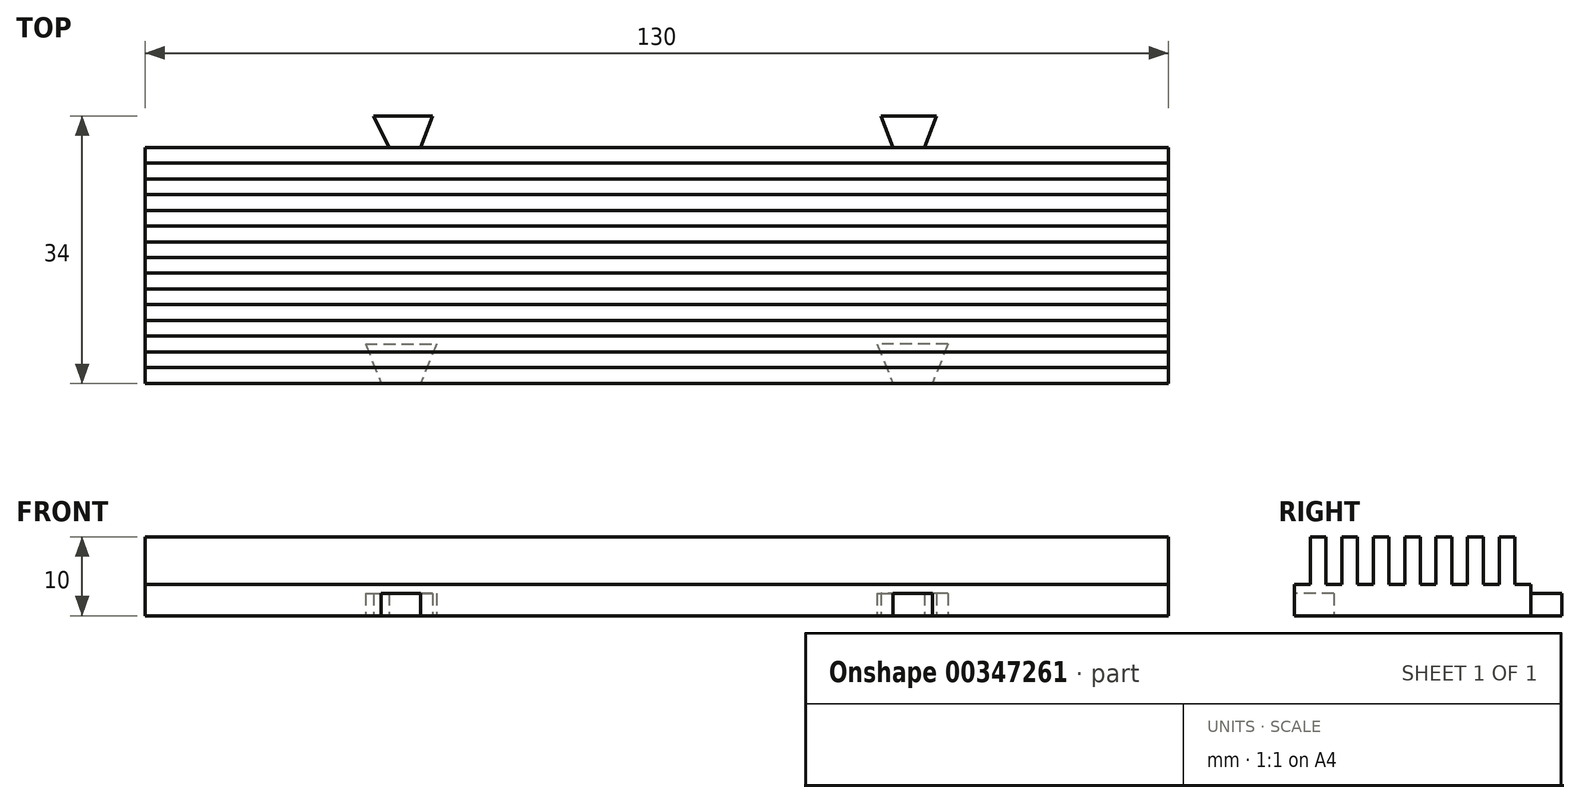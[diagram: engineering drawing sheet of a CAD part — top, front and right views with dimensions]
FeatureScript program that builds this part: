
annotation { "Feature Type Name" : "Feature", "Feature Type Description" : "" }
export const myFeature = defineFeature(function(context is Context, id is Id, definition is map)
    precondition{}
    {
        {
            var Q0;
            Q0=qCreatedBy(makeId("Top.planeOp"),FACE);
            var sketch = newSketch(context, id + "F0", { "sketchPlane" : qUnion([Q0])});
            skLineSegment(sketch, "E0.bottom", {"start": v(65, 15) * mm, "end": v(-65, 15) * mm});
            skLineSegment(sketch, "E0.top", {"start": v(65, -15) * mm, "end": v(-65, -15) * mm});
            skLineSegment(sketch, "E0.left", {"start": v(65, 15) * mm, "end": v(65, -15) * mm});
            skLineSegment(sketch, "E0.right", {"start": v(-65, 15) * mm, "end": v(-65, -15) * mm});
            skPoint(sketch, "E0.middle", {"position": v(0, 0) * mm});
            skSolve(sketch);
        }
        {
            var Q0;
            Q0=makeQuery(id+"F0.imprint","IMPRINT",FACE,{"disambiguationData":[TD([[makeQuery(id+"F0.imprint","IMPRINT",EDGE,{"derivedFrom":sQuery(id+"F0.wireOp",EDGE,"E0.bottom")}),1.0]])]});
            extrude(context, id + "F1", {"entities" : qUnion([Q0]), "depth" : 10 * mm});
        }
        {
            var Q0;
            Q0=makeQuery(id+"F1.opExtrude","CAP_FACE",FACE,{"disambiguationData":[OSD([sQuery(id+"F0.wireOp",EDGE,"E0.bottom"),sQuery(id+"F0.wireOp",EDGE,"E0.top"),sQuery(id+"F0.wireOp",EDGE,"E0.left"),sQuery(id+"F0.wireOp",EDGE,"E0.right")])],"isStart":false});
            var sketch = newSketch(context, id + "F2", { "sketchPlane" : qUnion([Q0])});
            skLineSegment(sketch, "E1", {"start": v(-65, -15) * mm, "end": v(-65, -13) * mm});
            skLineSegment(sketch, "E2", {"start": v(-65, -13) * mm, "end": v(65, -13) * mm});
            skLineSegment(sketch, "E3", {"start": v(65, -13) * mm, "end": v(65, -11) * mm});
            skLineSegment(sketch, "E4", {"start": v(65, -11) * mm, "end": v(-65, -11) * mm});
            skLineSegment(sketch, "E5", {"start": v(-65, -11) * mm, "end": v(-65, -9) * mm});
            skLineSegment(sketch, "E6", {"start": v(-65, -9) * mm, "end": v(65, -9) * mm});
            skLineSegment(sketch, "E7", {"start": v(65, -9) * mm, "end": v(65, -7) * mm});
            skLineSegment(sketch, "E8", {"start": v(65, -7) * mm, "end": v(-65, -7) * mm});
            skLineSegment(sketch, "E9", {"start": v(-65, -7) * mm, "end": v(-65, -5) * mm});
            skLineSegment(sketch, "E10", {"start": v(-65, -5) * mm, "end": v(65, -5) * mm});
            skLineSegment(sketch, "E11", {"start": v(65, -5) * mm, "end": v(65, -3) * mm});
            skLineSegment(sketch, "E12", {"start": v(65, -3) * mm, "end": v(-65, -3) * mm});
            skLineSegment(sketch, "E13", {"start": v(-65, -3) * mm, "end": v(-65, -1) * mm});
            skLineSegment(sketch, "E14", {"start": v(-65, -1) * mm, "end": v(65, -1) * mm});
            skLineSegment(sketch, "E15", {"start": v(65, -1) * mm, "end": v(65, 1) * mm});
            skLineSegment(sketch, "E16", {"start": v(65, 1) * mm, "end": v(-65, 1) * mm});
            skLineSegment(sketch, "E17", {"start": v(-65, 1) * mm, "end": v(-65, 3) * mm});
            skLineSegment(sketch, "E18", {"start": v(-65, 3) * mm, "end": v(65, 3) * mm});
            skLineSegment(sketch, "E19", {"start": v(65, 3) * mm, "end": v(65, 5) * mm});
            skLineSegment(sketch, "E20", {"start": v(65, 5) * mm, "end": v(-65, 5) * mm});
            skLineSegment(sketch, "E21", {"start": v(-65, 5) * mm, "end": v(-65, 7) * mm});
            skLineSegment(sketch, "E22", {"start": v(-65, 7) * mm, "end": v(65, 7) * mm});
            skLineSegment(sketch, "E23", {"start": v(65, 7) * mm, "end": v(65, 9) * mm});
            skLineSegment(sketch, "E24", {"start": v(65, 9) * mm, "end": v(-65, 9) * mm});
            skLineSegment(sketch, "E25", {"start": v(-65, 9) * mm, "end": v(-65, 11) * mm});
            skLineSegment(sketch, "E26", {"start": v(-65, 11) * mm, "end": v(65, 11) * mm});
            skLineSegment(sketch, "E27", {"start": v(65, 11) * mm, "end": v(65, 13) * mm});
            skLineSegment(sketch, "E28", {"start": v(65, 13) * mm, "end": v(-65, 13) * mm});
            skSolve(sketch);
        }
        {
            var Q0;
            Q0=makeQuery(id+"F2.imprint","IMPRINT",FACE,{"disambiguationData":[TD([[makeQuery(id+"F2.imprint","IMPRINT",EDGE,{"derivedFrom":sQuery(id+"F2.wireOp",EDGE,"E1")}),1.0]])]});
            var Q1;
            {var subQ0=sQuery(id+"F2.wireOp",EDGE,"E4");Q1=makeQuery(id+"F2.imprint","IMPRINT",FACE,{"disambiguationData":[TD([[makeQuery(id+"F2.imprint","IMPRINT",EDGE,{"derivedFrom":subQ0}),-1.0]])]});}
            var Q2;
            {var subQ0=sQuery(id+"F2.wireOp",EDGE,"E8");Q2=makeQuery(id+"F2.imprint","IMPRINT",FACE,{"disambiguationData":[TD([[makeQuery(id+"F2.imprint","IMPRINT",EDGE,{"derivedFrom":subQ0}),-1.0]])]});}
            var Q3;
            {var subQ0=sQuery(id+"F2.wireOp",EDGE,"E12");Q3=makeQuery(id+"F2.imprint","IMPRINT",FACE,{"disambiguationData":[TD([[makeQuery(id+"F2.imprint","IMPRINT",EDGE,{"derivedFrom":subQ0}),-1.0]])]});}
            var Q4;
            {var subQ0=sQuery(id+"F2.wireOp",EDGE,"E16");Q4=makeQuery(id+"F2.imprint","IMPRINT",FACE,{"disambiguationData":[TD([[makeQuery(id+"F2.imprint","IMPRINT",EDGE,{"derivedFrom":subQ0}),-1.0]])]});}
            var Q5;
            {var subQ0=sQuery(id+"F2.wireOp",EDGE,"E20");Q5=makeQuery(id+"F2.imprint","IMPRINT",FACE,{"disambiguationData":[TD([[makeQuery(id+"F2.imprint","IMPRINT",EDGE,{"derivedFrom":subQ0}),-1.0]])]});}
            var Q6;
            {var subQ0=sQuery(id+"F2.wireOp",EDGE,"E24");Q6=makeQuery(id+"F2.imprint","IMPRINT",FACE,{"disambiguationData":[TD([[makeQuery(id+"F2.imprint","IMPRINT",EDGE,{"derivedFrom":subQ0}),-1.0]])]});}
            var Q7;
            {var subQ0=sQuery(id+"F2.wireOp",EDGE,"E28");Q7=makeQuery(id+"F2.imprint","IMPRINT",FACE,{"disambiguationData":[TD([[makeQuery(id+"F2.imprint","IMPRINT",EDGE,{"derivedFrom":subQ0}),-1.0]])]});}
            extrude(context, id + "F3", {"entities" : qUnion([Q0, Q1, Q2, Q3, Q4, Q5, Q6, Q7]), "operationType" : NewBodyOperationType.REMOVE, "oppositeDirection" : true, "depth" : 6 * mm});
        }
        {
            var Q0;
            Q0=makeQuery(id+"F1.opExtrude","CAP_FACE",FACE,{"disambiguationData":[OSD([sQuery(id+"F0.wireOp",EDGE,"E0.bottom"),sQuery(id+"F0.wireOp",EDGE,"E0.top"),sQuery(id+"F0.wireOp",EDGE,"E0.left"),sQuery(id+"F0.wireOp",EDGE,"E0.right")])],"isStart":true});
            var sketch = newSketch(context, id + "F4", { "sketchPlane" : qUnion([Q0])});
            skLineSegment(sketch, "E29", {"start": v(-65, 15) * mm, "end": v(-35, 15) * mm});
            skLineSegment(sketch, "E30", {"start": v(-35, 15) * mm, "end": v(-30, 15) * mm});
            skLineSegment(sketch, "E31", {"start": v(-30, 15) * mm, "end": v(-30, 10) * mm});
            skLineSegment(sketch, "E32", {"start": v(-30, 10) * mm, "end": v(-28, 10) * mm});
            skLineSegment(sketch, "E33", {"start": v(-28, 10) * mm, "end": v(-30, 15) * mm});
            skLineSegment(sketch, "E34", {"start": v(-35, 15) * mm, "end": v(-35, 10) * mm});
            skLineSegment(sketch, "E35", {"start": v(-35, 10) * mm, "end": v(-37, 10) * mm});
            skLineSegment(sketch, "E36", {"start": v(-37, 10) * mm, "end": v(-35, 15) * mm});
            skLineSegment(sketch, "E37", {"start": v(-35, 10) * mm, "end": v(-30, 10) * mm});
            skLineSegment(sketch, "E38", {"start": v(65, 15) * mm, "end": v(35, 15) * mm});
            skLineSegment(sketch, "E39", {"start": v(35, 15) * mm, "end": v(30, 15) * mm});
            skLineSegment(sketch, "E40", {"start": v(30, 15) * mm, "end": v(30, 10) * mm});
            skLineSegment(sketch, "E41", {"start": v(30, 10) * mm, "end": v(28, 10) * mm});
            skLineSegment(sketch, "E42", {"start": v(28, 10) * mm, "end": v(30, 15) * mm});
            skLineSegment(sketch, "E43", {"start": v(35, 15) * mm, "end": v(35, 10) * mm});
            skLineSegment(sketch, "E44", {"start": v(35, 10) * mm, "end": v(37, 10) * mm});
            skLineSegment(sketch, "E45", {"start": v(37, 10) * mm, "end": v(35, 15) * mm});
            skLineSegment(sketch, "E46", {"start": v(35, 10) * mm, "end": v(30, 10) * mm});
            skLineSegment(sketch, "E47", {"start": v(-65, -15) * mm, "end": v(-34, -15) * mm});
            skLineSegment(sketch, "E48", {"start": v(-34, -15) * mm, "end": v(-30, -15) * mm});
            skLineSegment(sketch, "E49", {"start": v(-30, -15) * mm, "end": v(-30, -19) * mm});
            skLineSegment(sketch, "E50", {"start": v(-30, -19) * mm, "end": v(-28.5, -19) * mm});
            skLineSegment(sketch, "E51", {"start": v(-28.5, -19) * mm, "end": v(-30, -15) * mm});
            skLineSegment(sketch, "E52", {"start": v(-34, -15) * mm, "end": v(-34, -19) * mm});
            skLineSegment(sketch, "E53", {"start": v(-34, -19) * mm, "end": v(-36, -19) * mm});
            skLineSegment(sketch, "E54", {"start": v(-36, -19) * mm, "end": v(-34, -15) * mm});
            skLineSegment(sketch, "E55", {"start": v(-34, -19) * mm, "end": v(-30, -19) * mm});
            skLineSegment(sketch, "E56", {"start": v(65, -15) * mm, "end": v(34, -15) * mm});
            skLineSegment(sketch, "E57", {"start": v(34, -15) * mm, "end": v(30, -15) * mm});
            skLineSegment(sketch, "E58", {"start": v(30, -15) * mm, "end": v(30, -19) * mm});
            skLineSegment(sketch, "E59", {"start": v(30, -19) * mm, "end": v(28.5, -19) * mm});
            skLineSegment(sketch, "E60", {"start": v(28.5, -19) * mm, "end": v(30, -15) * mm});
            skLineSegment(sketch, "E61", {"start": v(34, -15) * mm, "end": v(34, -19) * mm});
            skLineSegment(sketch, "E62", {"start": v(34, -19) * mm, "end": v(35.5, -19) * mm});
            skLineSegment(sketch, "E63", {"start": v(35.5, -19) * mm, "end": v(34, -15) * mm});
            skLineSegment(sketch, "E64", {"start": v(34, -19) * mm, "end": v(30, -19) * mm});
            skSolve(sketch);
        }
        {
            var Q0;
            Q0=makeQuery(id+"F4.imprint","IMPRINT",FACE,{"disambiguationData":[TD([[makeQuery(id+"F4.imprint","IMPRINT",EDGE,{"derivedFrom":sQuery(id+"F4.wireOp",EDGE,"E30")}),1.0]])]});
            var Q1;
            Q1=makeQuery(id+"F4.imprint","IMPRINT",FACE,{"disambiguationData":[TD([[makeQuery(id+"F4.imprint","IMPRINT",EDGE,{"derivedFrom":sQuery(id+"F4.wireOp",EDGE,"E31")}),1.0]])]});
            var Q2;
            Q2=makeQuery(id+"F4.imprint","IMPRINT",FACE,{"disambiguationData":[TD([[makeQuery(id+"F4.imprint","IMPRINT",EDGE,{"derivedFrom":sQuery(id+"F4.wireOp",EDGE,"E34")}),-1.0]])]});
            var Q3;
            Q3=makeQuery(id+"F4.imprint","IMPRINT",FACE,{"disambiguationData":[TD([[makeQuery(id+"F4.imprint","IMPRINT",EDGE,{"derivedFrom":sQuery(id+"F4.wireOp",EDGE,"E39")}),1.0]])]});
            var Q4;
            Q4=makeQuery(id+"F4.imprint","IMPRINT",FACE,{"disambiguationData":[TD([[makeQuery(id+"F4.imprint","IMPRINT",EDGE,{"derivedFrom":sQuery(id+"F4.wireOp",EDGE,"E40")}),-1.0]])]});
            var Q5;
            Q5=makeQuery(id+"F4.imprint","IMPRINT",FACE,{"disambiguationData":[TD([[makeQuery(id+"F4.imprint","IMPRINT",EDGE,{"derivedFrom":sQuery(id+"F4.wireOp",EDGE,"E43")}),1.0]])]});
            extrude(context, id + "F5", {"entities" : qUnion([Q0, Q1, Q2, Q3, Q4, Q5]), "operationType" : NewBodyOperationType.REMOVE, "oppositeDirection" : true, "depth" : 2.8 * mm});
        }
        {
            var Q0;
            Q0=makeQuery(id+"F4.imprint","IMPRINT",FACE,{"disambiguationData":[TD([[makeQuery(id+"F4.imprint","IMPRINT",EDGE,{"derivedFrom":sQuery(id+"F4.wireOp",EDGE,"E57")}),1.0]])]});
            var Q1;
            Q1=makeQuery(id+"F4.imprint","IMPRINT",FACE,{"disambiguationData":[TD([[makeQuery(id+"F4.imprint","IMPRINT",EDGE,{"derivedFrom":sQuery(id+"F4.wireOp",EDGE,"E61")}),1.0]])]});
            var Q2;
            Q2=makeQuery(id+"F4.imprint","IMPRINT",FACE,{"disambiguationData":[TD([[makeQuery(id+"F4.imprint","IMPRINT",EDGE,{"derivedFrom":sQuery(id+"F4.wireOp",EDGE,"E58")}),-1.0]])]});
            var Q3;
            Q3=makeQuery(id+"F4.imprint","IMPRINT",FACE,{"disambiguationData":[TD([[makeQuery(id+"F4.imprint","IMPRINT",EDGE,{"derivedFrom":sQuery(id+"F4.wireOp",EDGE,"E48")}),1.0]])]});
            var Q4;
            Q4=makeQuery(id+"F4.imprint","IMPRINT",FACE,{"disambiguationData":[TD([[makeQuery(id+"F4.imprint","IMPRINT",EDGE,{"derivedFrom":sQuery(id+"F4.wireOp",EDGE,"E49")}),1.0]])]});
            var Q5;
            Q5=makeQuery(id+"F4.imprint","IMPRINT",FACE,{"disambiguationData":[TD([[makeQuery(id+"F4.imprint","IMPRINT",EDGE,{"derivedFrom":sQuery(id+"F4.wireOp",EDGE,"E52")}),-1.0]])]});
            extrude(context, id + "F6", {"entities" : qUnion([Q0, Q1, Q2, Q3, Q4, Q5]), "operationType" : NewBodyOperationType.ADD, "oppositeDirection" : true, "depth" : 2.8 * mm});
        }
    });
